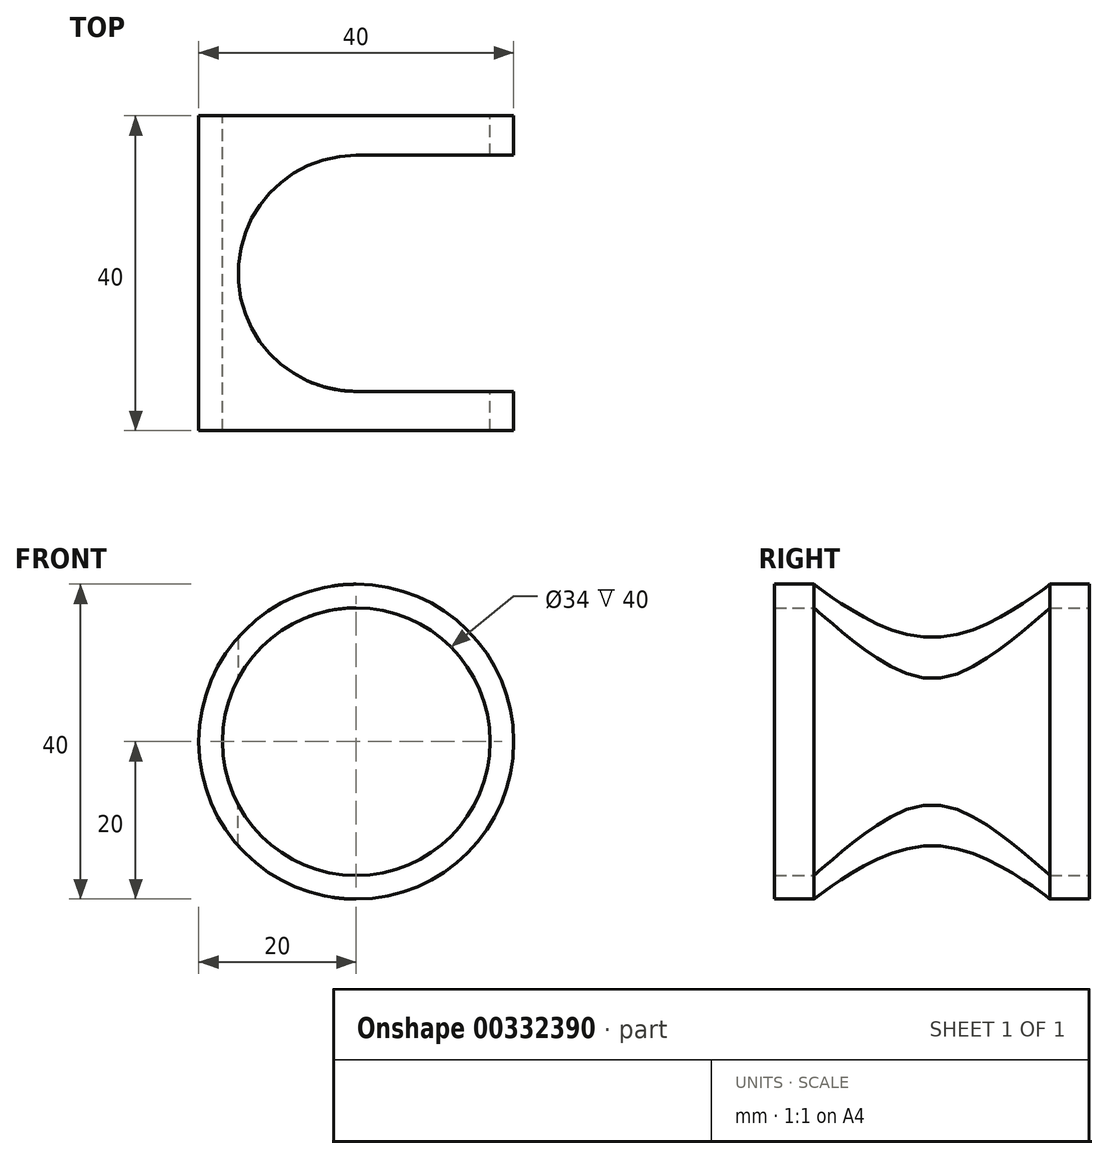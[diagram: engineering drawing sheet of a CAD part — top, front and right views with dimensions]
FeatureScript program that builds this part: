
annotation { "Feature Type Name" : "Feature", "Feature Type Description" : "" }
export const myFeature = defineFeature(function(context is Context, id is Id, definition is map)
    precondition{}
    {
        {
            var Q0;
            Q0=qCreatedBy(makeId("Front.planeOp"),FACE);
            var sketch = newSketch(context, id + "F0", { "sketchPlane" : qUnion([Q0])});
            skCircle(sketch, "E0", {"center": v(0, 0) * mm, "radius": 20 * mm});
            skCircle(sketch, "E1", {"center": v(0, 0) * mm, "radius": 17 * mm});
            skSolve(sketch);
        }
        {
            var Q0;
            Q0=makeQuery(id+"F0.imprint","IMPRINT",FACE,{"disambiguationData":[TD([[makeQuery(id+"F0.imprint","IMPRINT",EDGE,{"derivedFrom":sQuery(id+"F0.wireOp",EDGE,"E0")}),1.0]])]});
            extrude(context, id + "F1", {"entities" : qUnion([Q0]), "depth" : 40 * mm});
        }
        {
            var Q0;
            Q0=qCreatedBy(makeId("Top.planeOp"),FACE);
            var sketch = newSketch(context, id + "F2", { "sketchPlane" : qUnion([Q0])});
            skArc(sketch, "E2", {"start": v(0, -5) * mm, "mid": v(-15, -20) * mm, "end": v(0, -35) * mm});
            skArc(sketch, "E3", {"start": v(20, -35) * mm, "mid": v(35, -20) * mm, "end": v(20, -5) * mm});
            skLineSegment(sketch, "E4", {"start": v(0, -5) * mm, "end": v(20, -5) * mm});
            skLineSegment(sketch, "E5", {"start": v(0, -35) * mm, "end": v(20, -35) * mm});
            skSolve(sketch);
        }
        {
            var Q0;
            Q0=makeQuery(id+"F2.imprint","IMPRINT",FACE,{"disambiguationData":[TD([[makeQuery(id+"F2.imprint","IMPRINT",EDGE,{"derivedFrom":sQuery(id+"F2.wireOp",EDGE,"E2")}),1.0]])]});
            extrude(context, id + "F3", {"entities" : qUnion([Q0]), "operationType" : NewBodyOperationType.REMOVE, "depth" : 25 * mm});
        }
        {
            var Q0;
            Q0 = qSketchRegion(id + "F2", true);
            extrude(context, id + "F4", {"entities" : qUnion([Q0]), "operationType" : NewBodyOperationType.REMOVE, "oppositeDirection" : true, "depth" : 25 * mm});
        }
    });
